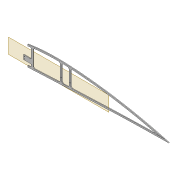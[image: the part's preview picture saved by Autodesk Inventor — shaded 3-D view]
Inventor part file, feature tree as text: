
AUTODESK INVENTOR PART (.ipt)
format: ipt  version: 2022 (Build 260153000, 153)  size: 568,320 bytes
history: native  units: mm
features: extrude x9, sketch x9, projected_geometry x9, fillet x2, shell x1, plane x1, chamfer x1
ambient origin geometry x8: Origin, YZ Plane, XZ Plane, XY Plane, X Axis, Y Axis, Z Axis, Center Point
bodies: Solid1 (feature_tree)
feature tree (32):
  extrude  "Extrusion1"  Depth=4.0mm
  shell  "Shell1"  Thickness=2.0mm
  extrude  "Extrusion8"  Depth=5.9mm
  extrude  "Extrusion3"  Depth=10.0mm TaperAngle=0.0deg
  extrude  "Extrusion4"  Depth=2.0mm
  fillet  "Fillet1"  Radius=5.0mm
  sketch  "Sketch10"  dims[d22=2.0mm d23=0.0mm d31=2.0mm d32=5.0mm]
  extrude  "Extrusion5"  Depth=2.5mm
  plane  "Work Plane2"
  extrude  "Extrusion9"  Depth=1.6mm
  extrude  "Extrusion10"  Depth=80.0mm
  fillet  "Fillet2"  Radius=6.0mm
  extrude  "Extrusion11"  Depth=3.0mm
  chamfer  "Chamfer1"  Distance=5.0mm
  extrude  "Extrusion13"  Depth=22.0mm
  sketch  "Sketch30"  dims[d64=2.0mm d65=0.0mm d66=3.0mm]
  sketch  "Sketch31"  dims[d67=12.0mm d68=5.0mm d69=22.0mm d70=12.0mm d71=3.05mm d72=2.0mm d73=0.0mm d74=10.0mm d75=0.0mm d76=2.0mm d77=100.0mm d78=20.0mm d79=0.5mm d80=10.0mm d81=0.0mm d84=10.0mm d85=10.0mm d87=3.0mm d88=2.0mm d89=45.0deg d90=1.0mm d91=1.0mm d92=1.0mm d93=1.0mm d94=1.0mm d95=1.0mm d96=10.0mm d97=0.0mm]
  sketch  "Sketch3"  dims[d0=2.0mm d1=0.0mm d2=4.0mm d7=2.0mm]
  sketch  "Sketch8"  dims[d8=2.0mm d9=5.9mm]
  sketch  "Sketch9"  dims[d13=10.0mm d14=0.0mm d16=10.0mm d17=0.0mm]
  projected_geometry  "Projected Loop4"
  projected_geometry  "Projected Loop10"
  sketch  "Sketch24"  dims[d34=1.6mm d35=2.5mm]
  projected_geometry  "Projected Loop11"
  projected_geometry  "Projected Loop12"
  sketch  "Sketch26"  dims[d37=5.0mm d38=1.6mm]
  projected_geometry  "Projected Loop13"
  sketch  "Sketch29"  dims[d40=2.5mm d62=80.0mm d63=6.0mm]
  projected_geometry  "Project Cut Edges1"
  projected_geometry  "Project Cut Edges3"
  projected_geometry  "Project Cut Edges4"
  projected_geometry  "Project Cut Edges5"
